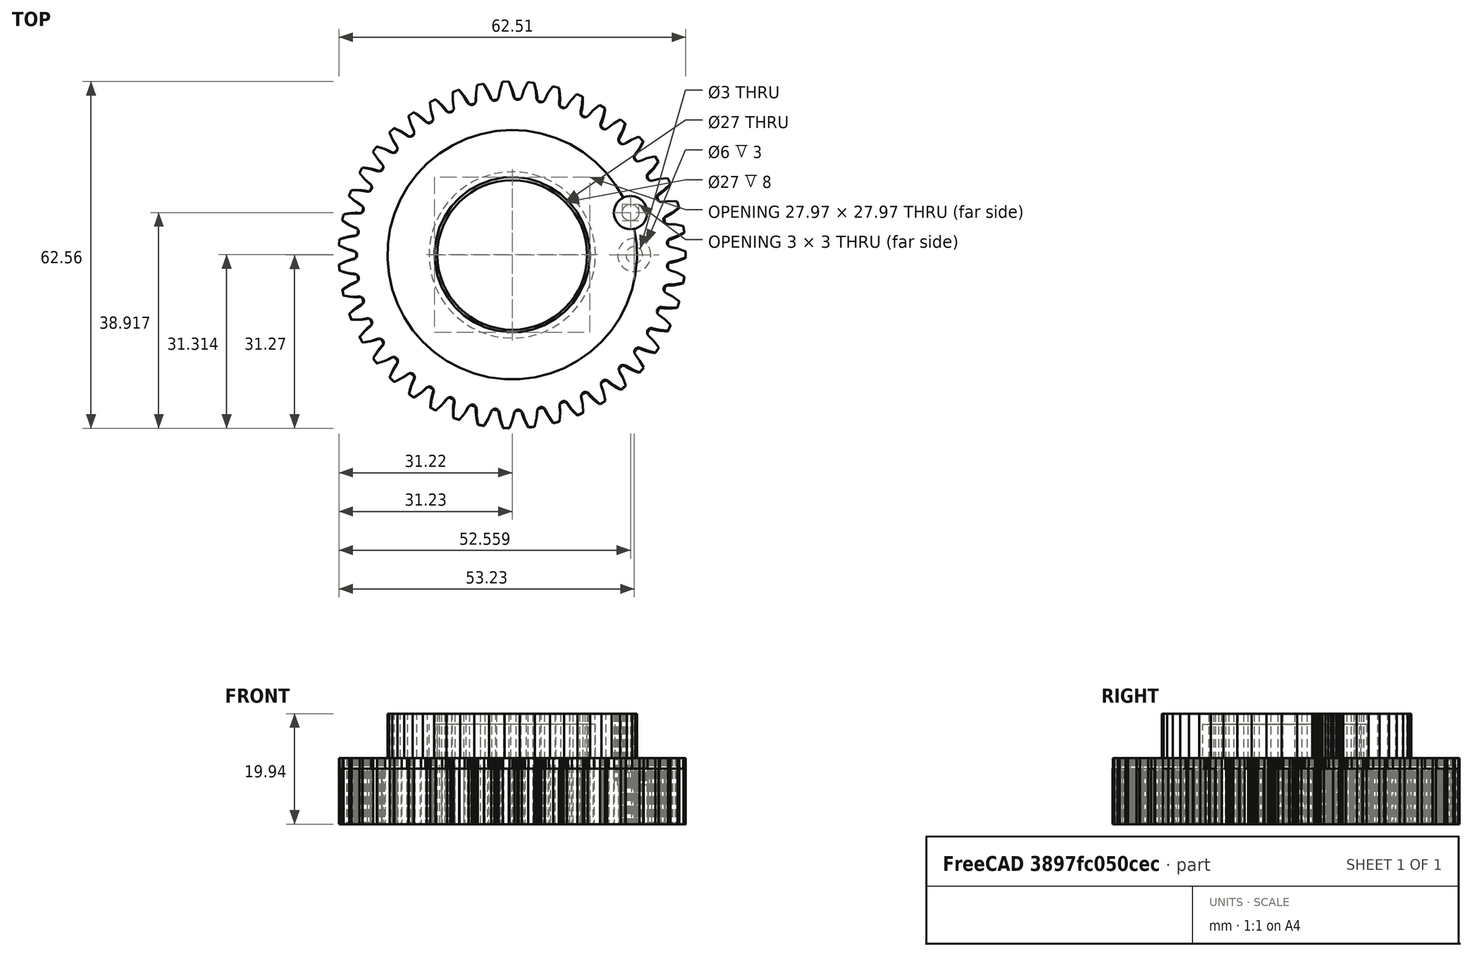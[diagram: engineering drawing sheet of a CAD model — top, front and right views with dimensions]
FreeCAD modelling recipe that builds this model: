
FCSTD DOCUMENT  (FreeCAD 0.15R4671 (Git))
Label: cad
License: All rights reserved
LicenseURL: http://en.wikipedia.org/wiki/All_rights_reserved
objects: Part::Cut×4, Part::Cylinder×4, Part::Part2DObjectPython×2, Part::Feature×1, PartDesign::Pad×1, Part::Extrusion×1, Part::MultiFuse×1
note: 15 computed .brp shape members not serialized (recipe doc carries the construction recipe); baked Part::Feature solids carry a one-line shape summary decoded from their .brp

FEATURE [Part::Feature] Solid
  Placement = pos=(-0.8,1.45,0) rot=(0,0,1;0.111701rad)
  shape: bbox 62.46 x 62.5 x 19.94 mm, 1162 faces (baked)
FEATURE [Part::Part2DObjectPython] InvoluteGear001  # Draft 2D object (typed FeaturePython)
  ExternalGear = true
  HighPrecision = true
  Modules = 1.39
  NumberOfTeeth = 43
  PressureAngle = 20
FEATURE [PartDesign::Pad] Pad001
  Length = 10
  Length2 = 100
  Sketch = -> InvoluteGear001
  Type = 0
FEATURE [Part::Part2DObjectPython] Circle001  # Draft 2D object (typed FeaturePython)
  FirstAngle = 0
  LastAngle = 0
  MakeFace = false
  Placement = pos=(0,0,12) rot=(0,0,1;0rad)
  Radius = 13.5
FEATURE [Part::Extrusion] Extrude001
  Base = -> Circle001
  Dir = (0,0,-12)
  Solid = false
FEATURE [Part::Cut] Cut002
  Base = -> Pad001
  Tool = -> Extrude001
FEATURE [Part::Cylinder] Cylinder002
  Angle = 360
  Height = 8
  Placement = pos=(0,0,10) rot=(0,0,1;0rad)
  Radius = 15
FEATURE [Part::Cylinder] Cylinder003
  Angle = 360
  Height = 8
  Placement = pos=(0,0,10) rot=(0,0,1;0rad)
  Radius = 13.5
FEATURE [Part::Cut] Cut003
  Base = -> Cylinder002
  Tool = -> Cylinder003
FEATURE [Part::Cylinder] Cylinder
  Angle = 360
  Height = 10
  Placement = pos=(22,0,0) rot=(0,0,1;0rad)
  Radius = 1.5
FEATURE [Part::Cut] Cut
  Base = -> Cut002
  Tool = -> Cylinder
FEATURE [Part::Cylinder] Cylinder004
  Angle = 360
  Height = 3
  Placement = pos=(22,0,7) rot=(0,0,1;0rad)
  Radius = 3
FEATURE [Part::Cut] Cut004
  Base = -> Cut
  Tool = -> Cylinder004
FEATURE [Part::MultiFuse] Fusion
  Shapes = -> [Cut004,Cut003]
